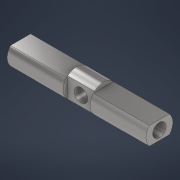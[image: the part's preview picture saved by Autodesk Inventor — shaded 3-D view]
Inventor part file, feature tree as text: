
AUTODESK INVENTOR PART (.ipt)
format: ipt  version: 2022 (Build 260153000, 153)  size: 152,064 bytes
history: native  units: mm
features: extrude x5, sketch x5, move_body x2, direct_edit x1, projected_geometry x1
ambient origin geometry x8: Origin, YZ Plane, XZ Plane, XY Plane, X Axis, Y Axis, Z Axis, Center Point
bodies: Solid1 (feature_tree)
feature tree (14):
  extrude  "Extrusion1"  Depth=31.0mm TaperAngle=0.0deg
  extrude  "Extrusion2"  Depth=7.0mm
  extrude  "Extrusion3"  Depth=6.0mm TaperAngle=0.0deg
  extrude  "Extrusion4"  TaperAngle=0.0deg  [1 undecoded]
  extrude  "Extrusion5"  Depth=4.0mm
  direct_edit  "Direct Edit1"
  sketch  "Sketch1"  dims[d0=6.0mm d1=31.0mm d2=0.0mm]
  sketch  "Sketch2"  dims[d3=1.0mm d4=7.0mm]
  sketch  "Sketch3"  dims[d5=1.0mm d6=6.0mm d7=0.0mm]
  sketch  "Sketch4"  dims[d8=3.0mm d9=0.0mm d10=0.0mm]
  sketch  "Sketch5"  dims[d11=3.0mm d12=6.0mm d13=6.0mm d14=4.0mm d15=5.5mm d16=0.0mm d17=6.0mm d18=5.5mm d19=0.0mm d20=0.0mm d21=0.0mm d22=-7.0mm d23=0.0mm d24=0.0mm d25=-7.0mm]
  projected_geometry  "Projected Loop1"
  move_body  "Move1"
  move_body  "Move2"
note: 1 required parameter value undecoded (feature->parameter linkage not recoverable at this tier; creation-order binding heuristic only, values carry confidence <= 0.55)
